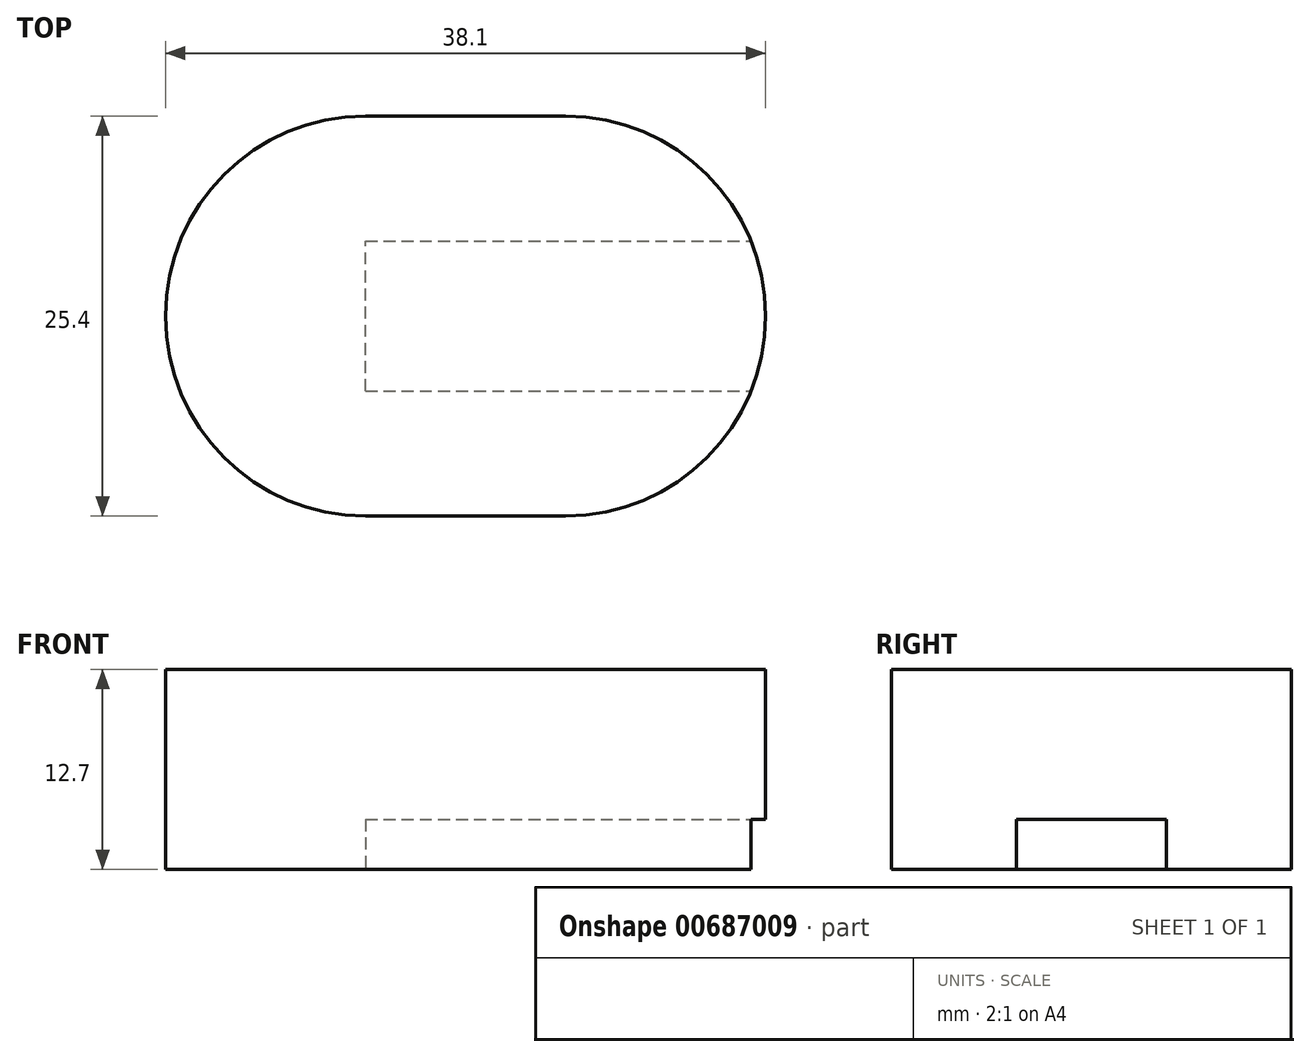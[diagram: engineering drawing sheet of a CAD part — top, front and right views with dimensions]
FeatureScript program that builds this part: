
annotation { "Feature Type Name" : "Feature", "Feature Type Description" : "" }
export const myFeature = defineFeature(function(context is Context, id is Id, definition is map)
    precondition{}
    {
        {
            var Q0;
            Q0=qCreatedBy(makeId("Top.planeOp"),FACE);
            var sketch = newSketch(context, id + "F0", { "sketchPlane" : qUnion([Q0])});
            skCircle(sketch, "E0", {"center": v(0, 0) * mm, "radius": 12.7 * mm});
            skCircle(sketch, "E1", {"center": v(12.7, 0) * mm, "radius": 12.7 * mm});
            skLineSegment(sketch, "E2.bottom", {"start": v(0, 0) * mm, "end": v(12.7, 0) * mm});
            skLineSegment(sketch, "E2.top", {"start": v(0, 12.7) * mm, "end": v(12.7, 12.7) * mm});
            skLineSegment(sketch, "E2.left", {"start": v(0, 0) * mm, "end": v(0, 12.7) * mm});
            skLineSegment(sketch, "E2.right", {"start": v(12.7, 0) * mm, "end": v(12.7, 12.7) * mm});
            skLineSegment(sketch, "E3.top", {"start": v(0, -12.7) * mm, "end": v(12.7, -12.7) * mm});
            skLineSegment(sketch, "E3.left", {"start": v(0, 0) * mm, "end": v(0, -12.7) * mm});
            skLineSegment(sketch, "E3.right", {"start": v(12.7, 0) * mm, "end": v(12.7, -12.7) * mm});
            skSolve(sketch);
        }
        {
            var Q0;
            {var subQ0=sQuery(id+"F0.wireOp",EDGE,"E2.left");Q0=makeQuery(id+"F0.imprint","IMPRINT",FACE,{"disambiguationData":[TD([[makeQuery(id+"F0.imprint","IMPRINT",EDGE,{"derivedFrom":subQ0}),1.0]])]});}
            var Q1;
            {var subQ0=sQuery(id+"F0.wireOp",EDGE,"E2.bottom");Q1=makeQuery(id+"F0.imprint","IMPRINT",FACE,{"disambiguationData":[TD([[makeQuery(id+"F0.imprint","IMPRINT",EDGE,{"derivedFrom":subQ0}),-1.0]])]});}
            var Q2;
            {var subQ0=sQuery(id+"F0.wireOp",EDGE,"E3.left");Q2=makeQuery(id+"F0.imprint","IMPRINT",FACE,{"disambiguationData":[TD([[makeQuery(id+"F0.imprint","IMPRINT",EDGE,{"derivedFrom":subQ0}),1.0]])]});}
            var Q3;
            {var subQ0=sQuery(id+"F0.wireOp",EDGE,"E2.left");Q3=makeQuery(id+"F0.imprint","IMPRINT",FACE,{"disambiguationData":[TD([[makeQuery(id+"F0.imprint","IMPRINT",EDGE,{"derivedFrom":subQ0}),-1.0]])]});}
            var Q4;
            {var subQ0=sQuery(id+"F0.wireOp",EDGE,"E2.bottom");Q4=makeQuery(id+"F0.imprint","IMPRINT",FACE,{"disambiguationData":[TD([[makeQuery(id+"F0.imprint","IMPRINT",EDGE,{"derivedFrom":subQ0}),1.0]])]});}
            var Q5;
            {var subQ0=sQuery(id+"F0.wireOp",EDGE,"E2.right");Q5=makeQuery(id+"F0.imprint","IMPRINT",FACE,{"disambiguationData":[TD([[makeQuery(id+"F0.imprint","IMPRINT",EDGE,{"derivedFrom":subQ0}),1.0]])]});}
            var Q6;
            {var subQ0=sQuery(id+"F0.wireOp",EDGE,"E2.right");Q6=makeQuery(id+"F0.imprint","IMPRINT",FACE,{"disambiguationData":[TD([[makeQuery(id+"F0.imprint","IMPRINT",EDGE,{"derivedFrom":subQ0}),-1.0]])]});}
            var Q7;
            {var subQ0=sQuery(id+"F0.wireOp",EDGE,"E3.top");Q7=makeQuery(id+"F0.imprint","IMPRINT",FACE,{"disambiguationData":[TD([[makeQuery(id+"F0.imprint","IMPRINT",EDGE,{"derivedFrom":subQ0}),1.0]])]});}
            var Q8;
            {var subQ0=sQuery(id+"F0.wireOp",EDGE,"E2.top");Q8=makeQuery(id+"F0.imprint","IMPRINT",FACE,{"disambiguationData":[TD([[makeQuery(id+"F0.imprint","IMPRINT",EDGE,{"derivedFrom":subQ0}),-1.0]])]});}
            var Q9;
            {var subQ0=sQuery(id+"F0.wireOp",EDGE,"E3.right");Q9=makeQuery(id+"F0.imprint","IMPRINT",FACE,{"disambiguationData":[TD([[makeQuery(id+"F0.imprint","IMPRINT",EDGE,{"derivedFrom":subQ0}),-1.0]])]});}
            extrude(context, id + "F1", {"entities" : qUnion([Q0, Q1, Q2, Q3, Q4, Q5, Q6, Q7, Q8, Q9]), "depth" : 12.7 * mm, "offsetDistance" : 25.4 * mm});
        }
        {
            var Q0;
            Q0=qCreatedBy(makeId("Top.planeOp"),FACE);
            var sketch = newSketch(context, id + "F2", { "sketchPlane" : qUnion([Q0])});
            skLineSegment(sketch, "E4.left", {"start": v(0, 0) * mm, "end": v(0, -4.76) * mm});
            skLineSegment(sketch, "E5.bottom", {"start": v(0, -4.76) * mm, "end": v(25.4, -4.76) * mm});
            skLineSegment(sketch, "E5.top", {"start": v(0, 4.76) * mm, "end": v(25.4, 4.76) * mm});
            skLineSegment(sketch, "E5.left", {"start": v(0, -4.76) * mm, "end": v(0, 4.76) * mm});
            skLineSegment(sketch, "E5.right", {"start": v(25.4, -4.76) * mm, "end": v(25.4, 4.76) * mm});
            skSolve(sketch);
        }
        {
            var Q0;
            Q0 = qSketchRegion(id + "F2", true);
            extrude(context, id + "F3", {"entities" : qUnion([Q0]), "operationType" : NewBodyOperationType.REMOVE, "depth" : 3.17 * mm, "offsetDistance" : 25.4 * mm});
        }
    });
